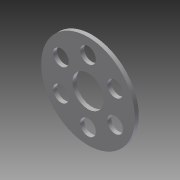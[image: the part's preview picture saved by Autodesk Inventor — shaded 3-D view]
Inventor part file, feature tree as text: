
AUTODESK INVENTOR PART (.ipt)
format: ipt  version: 2014 (Build 180170000, 170)  size: 105,984 bytes
history: native  units: in
note: dims shown in document units (in); Inventor stores cm internally (conversion verified against a paired STEP export)
features: sheet_metal_op x1, sketch x1, other x1
ambient origin geometry x8: Origin, YZ Plane, XZ Plane, XY Plane, X Axis, Y Axis, Z Axis, Center Point
bodies: Solid1 (feature_tree)
feature tree (3):
  sheet_metal_op  "Face1"
  sketch  "Sketch1"  dims[d0=3.0in d1=1.0in d2=0.5in d3=1.0in d4=2.3622in d6=360.0deg d8=0.125in]
  other  "Plate1"
